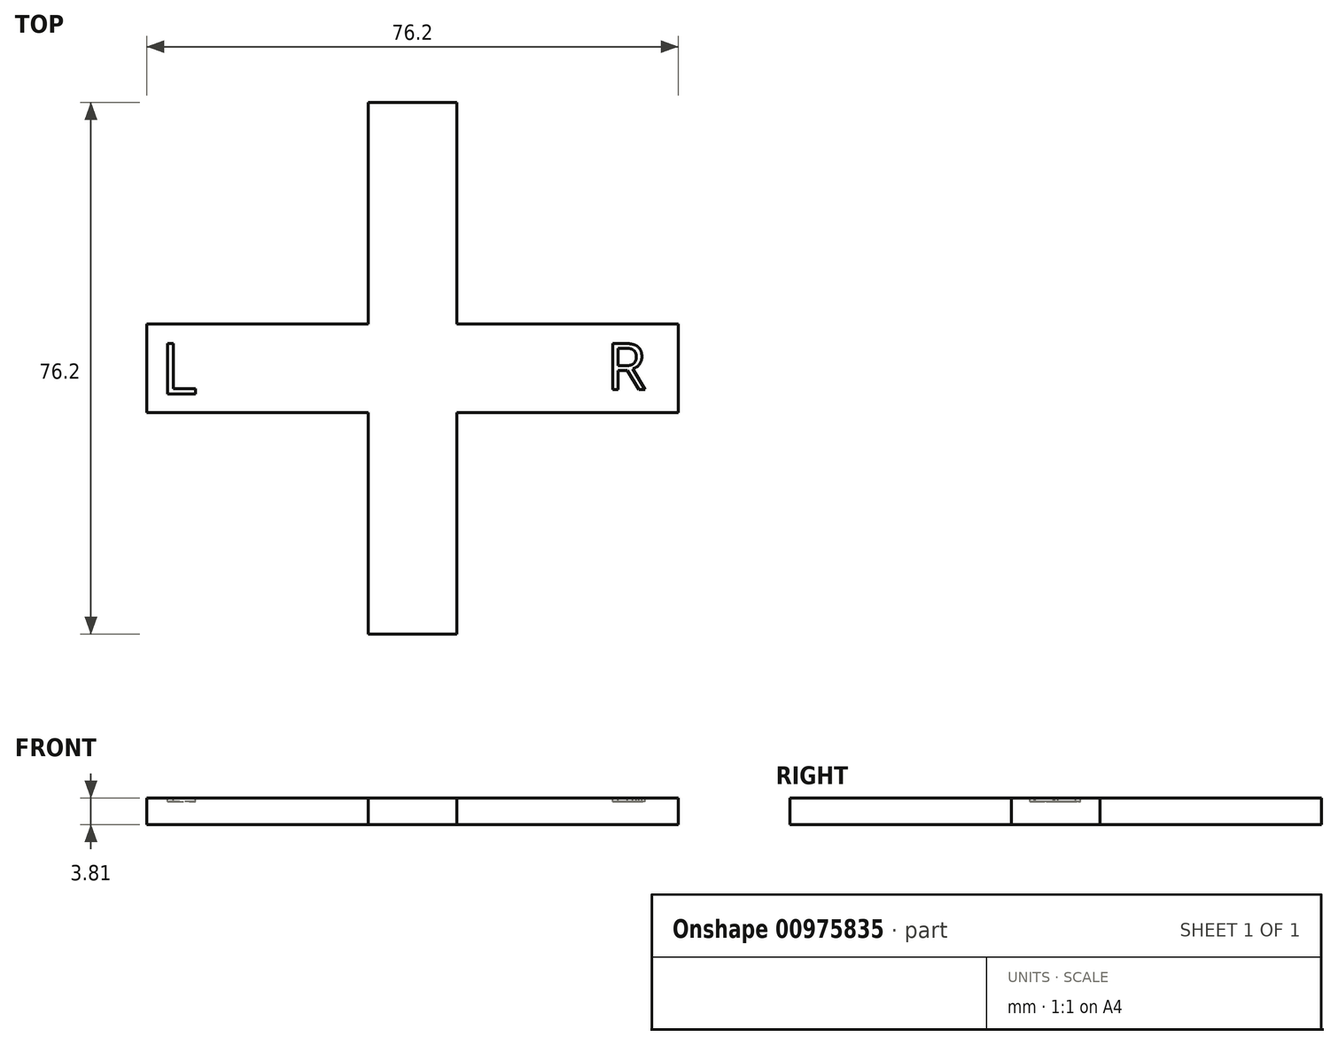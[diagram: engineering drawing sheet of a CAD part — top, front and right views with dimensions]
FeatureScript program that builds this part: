
annotation { "Feature Type Name" : "Feature", "Feature Type Description" : "" }
export const myFeature = defineFeature(function(context is Context, id is Id, definition is map)
    precondition{}
    {
        {
            var Q0;
            Q0=qCreatedBy(makeId("Top.planeOp"),FACE);
            var sketch = newSketch(context, id + "F0", { "sketchPlane" : qUnion([Q0])});
            skLineSegment(sketch, "E0", {"start": v(0, 38.1) * mm, "end": v(0, -38.1) * mm, "construction": true});
            skLineSegment(sketch, "E1", {"start": v(-38.1, -6.35) * mm, "end": v(0, -6.35) * mm});
            skLineSegment(sketch, "E2", {"start": v(0, -6.35) * mm, "end": v(38.1, -6.35) * mm});
            skLineSegment(sketch, "E3", {"start": v(38.1, 6.35) * mm, "end": v(38.1, -6.35) * mm});
            skLineSegment(sketch, "E4", {"start": v(38.1, 6.35) * mm, "end": v(0, 6.35) * mm});
            skLineSegment(sketch, "E5", {"start": v(0, 6.35) * mm, "end": v(-38.1, 6.35) * mm});
            skLineSegment(sketch, "E6", {"start": v(-38.1, -6.35) * mm, "end": v(-38.1, 6.35) * mm});
            skLineSegment(sketch, "E7", {"start": v(-6.35, -6.35) * mm, "end": v(-6.35, 38.1) * mm});
            skLineSegment(sketch, "E8", {"start": v(-6.35, 38.1) * mm, "end": v(6.35, 38.1) * mm});
            skLineSegment(sketch, "E9", {"start": v(6.35, 38.1) * mm, "end": v(6.35, -6.35) * mm});
            skLineSegment(sketch, "E10", {"start": v(-6.35, 6.35) * mm, "end": v(-6.35, -38.1) * mm});
            skLineSegment(sketch, "E11", {"start": v(-6.35, -38.1) * mm, "end": v(6.35, -38.1) * mm});
            skLineSegment(sketch, "E12", {"start": v(6.35, -38.1) * mm, "end": v(6.35, 6.35) * mm});
            skLineSegment(sketch, "E13", {"start": v(-38.1, 0) * mm, "end": v(38.1, 0) * mm, "construction": true});
            skSolve(sketch);
        }
        {
            var Q0;
            Q0 = qSketchRegion(id + "F0", true);
            extrude(context, id + "F1", {"entities" : qUnion([Q0]), "depth" : 3.8 * mm, "offsetDistance" : 25.4 * mm});
        }
        {
            var Q0;
            Q0=makeQuery(id+"F1.opExtrude","CAP_FACE",FACE,{"disambiguationData":[OSD([sQuery(id+"F0.wireOp",EDGE,"E1"),sQuery(id+"F0.wireOp",EDGE,"E2"),sQuery(id+"F0.wireOp",EDGE,"E3"),sQuery(id+"F0.wireOp",EDGE,"E4"),sQuery(id+"F0.wireOp",EDGE,"E5"),sQuery(id+"F0.wireOp",EDGE,"E6"),sQuery(id+"F0.wireOp",EDGE,"E7"),sQuery(id+"F0.wireOp",EDGE,"E8"),sQuery(id+"F0.wireOp",EDGE,"E9"),sQuery(id+"F0.wireOp",EDGE,"E10"),sQuery(id+"F0.wireOp",EDGE,"E11"),sQuery(id+"F0.wireOp",EDGE,"E12")])],"isStart":false});
            var sketch = newSketch(context, id + "F2", { "sketchPlane" : qUnion([Q0])});
            skText(sketch, "E14", { "text": "L", "fontName": "OpenSans-Regular.ttf"});
            skText(sketch, "E15", { "text": "R", "fontName": "OpenSans-Regular.ttf"});
            const initialGuessF2  = {"E14": [-0.03613, -0.00366, 1, 0, 0.00725], "E15": [0.02776, -0.00307, 1, 0, 0.00668]};
            skSetInitialGuess(sketch, initialGuessF2);
            skSolve(sketch);
        }
        {
            var Q0;
            Q0 = qSketchRegion(id + "F2", true);
            extrude(context, id + "F3", {"entities" : qUnion([Q0]), "operationType" : NewBodyOperationType.REMOVE, "oppositeDirection" : true, "depth" : 0.5 * mm, "offsetDistance" : 25.4 * mm});
        }
    });
